# Revit family: Safety_Encon-Safety_Galvanized-Pipe-30-gpm-Shower-8.0-Eye-Facewash
name_source: partatom
category: Plumbing Fixtures
units: mm (PartAtom-declared; Revit-internal decimal feet)

## family parameters
Always vertical = Yes
Cut with Voids When Loaded = No
OmniClass Number = 23.45.05.14.24
Part Type = Normal
Room Calculation Point = No
Round Connector Dimension = Use Diameter
Shared = No
Work Plane-Based = No

## types (1)
- 01050216
    Assembly Code = D2010600
    CW Connection = Yes
    CWFU = 0
    Description = Galvanized Pipe 30 gpm Shower, 8.0 gpm Eye/Facewash
    Drain Type = FNPT
    Edition number = 1
    Flow = 38 GPM
    Fluid out Diameter = 1 1/2"
    HW Connection = No
    HWFU = 0
    Heads Material = Encon Safety Products - Plastic - Acetal - Yellow
    Height = 94 1/2"
    Keynote = 15410
    Manufacturer = Encon Safety Products
    Model = 01050216
    Pedestal Material = Encon Safety Products - Metal - Steel Galvanized
    Piping Material = Encon Safety Products - Plastic - PVC - Black
    Product Guid = c2eda6dc-bce4-4d89-8ddb-28141d08e67f
    Product data url = https://www.bimobject.com
    Supply Diameter = 1 1/2"
    URL = https://enconsafety.com
    Vent Connection = No
    WFU = 0
    Waste Connection = Yes
    Width = 24"

## geometry (parser evidence)
native form markers: Sweep x1
no freeform markers — native parametric forms only
